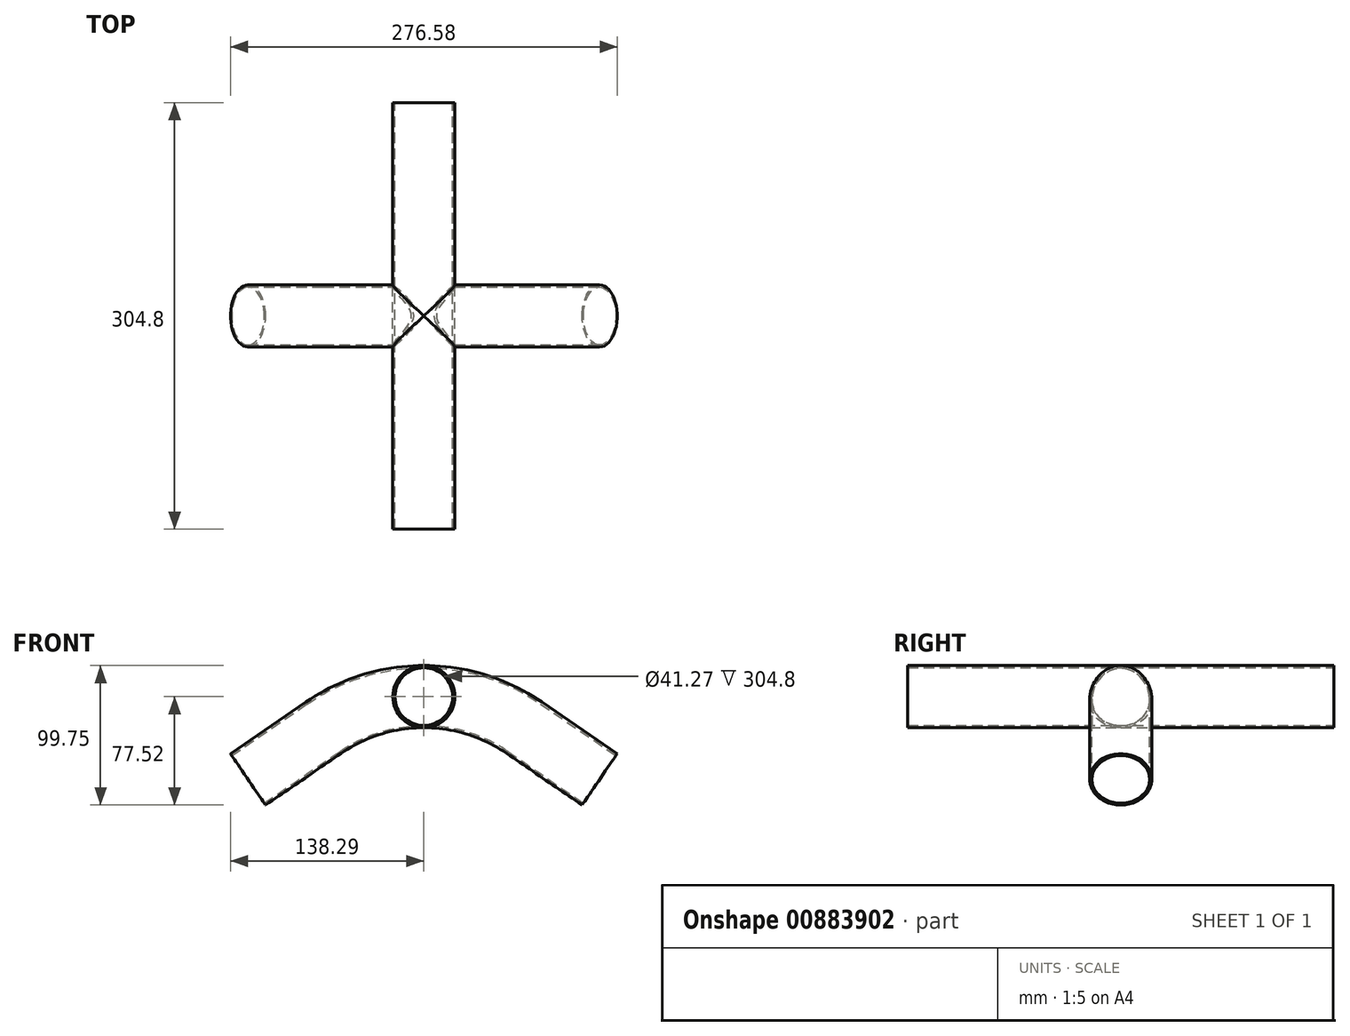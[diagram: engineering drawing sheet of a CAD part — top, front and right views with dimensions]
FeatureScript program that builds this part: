
annotation { "Feature Type Name" : "Feature", "Feature Type Description" : "" }
export const myFeature = defineFeature(function(context is Context, id is Id, definition is map)
    precondition{}
    {
        {
            var Q0;
            Q0=qCreatedBy(makeId("Front.planeOp"),FACE);
            var sketch = newSketch(context, id + "F0", { "sketchPlane" : qUnion([Q0])});
            skCircle(sketch, "E0", {"center": v(0, 0) * mm, "radius": 20.64 * mm});
            skCircle(sketch, "E1.0", {"center": v(0, 0) * mm, "radius": 22.23 * mm});
            skSolve(sketch);
        }
        {
            var Q0;
            Q0=makeQuery(id+"F0.imprint","IMPRINT",FACE,{"disambiguationData":[TD([[makeQuery(id+"F0.imprint","IMPRINT",EDGE,{"derivedFrom":sQuery(id+"F0.wireOp",EDGE,"E0")}),-1.0]])]});
            extrude(context, id + "F1", {"entities" : qUnion([Q0]), "endBound" : BoundingType.SYMMETRIC, "depth" : 304.8 * mm, "offsetDistance" : 25.4 * mm});
        }
        {
            var Q0;
            Q0=qCreatedBy(makeId("Front.planeOp"),FACE);
            var sketch = newSketch(context, id + "F2", { "sketchPlane" : qUnion([Q0])});
            skLineSegment(sketch, "E2", {"start": v(-125.73, -59.19) * mm, "end": v(-71.77, -22.23) * mm});
            skArc(sketch, "E3", {"start": v(-71.77, -22.23) * mm, "mid": v(0, 0) * mm, "end": v(71.77, -22.23) * mm});
            skLineSegment(sketch, "E4", {"start": v(71.77, -22.23) * mm, "end": v(125.73, -59.19) * mm});
            skLineSegment(sketch, "E5", {"start": v(-71.77, -22.23) * mm, "end": v(0, 26.94) * mm, "construction": true});
            skLineSegment(sketch, "E6", {"start": v(0, 26.94) * mm, "end": v(71.77, -22.23) * mm, "construction": true});
            skSolve(sketch);
        }
        {
            var Q0;
            Q0=sQuery(id+"F2.wireOp",VERTEX,"E2.start");
            var Q1;
            Q1=sQuery(id+"F2.wireOp",EDGE,"E2");
            cPlane(context, id + "F3", {"entities" : qUnion([Q0, Q1]), "cplaneType" : CPlaneType.LINE_POINT, "offset" : 25.4 * mm, "width" : 152.4 * mm, "height" : 152.4 * mm});
        }
        {
            var Q0;
            Q0=qCreatedBy(id+"F3.planeOp",FACE);
            var sketch = newSketch(context, id + "F4", { "sketchPlane" : qUnion([Q0])});
            skCircle(sketch, "E7", {"center": v(0, 22.23) * mm, "radius": 20.64 * mm});
            skCircle(sketch, "E8.0", {"center": v(0, 22.23) * mm, "radius": 22.23 * mm});
            skSolve(sketch);
        }
        {
            var Q0;
            Q0=makeQuery(id+"F4.imprint","IMPRINT",FACE,{"disambiguationData":[TD([[makeQuery(id+"F4.imprint","IMPRINT",EDGE,{"derivedFrom":sQuery(id+"F4.wireOp",EDGE,"E7")}),-1.0]])]});
            var Q1;
            Q1=sQuery(id+"F2.wireOp",EDGE,"E2");
            var Q2;
            Q2=sQuery(id+"F2.wireOp",EDGE,"E3");
            var Q3;
            Q3=sQuery(id+"F2.wireOp",EDGE,"E4");
            sweep(context, id + "F5", {"operationType" : NewBodyOperationType.ADD, "profiles" : qUnion([Q0]), "path" : qUnion([Q1, Q2, Q3])});
        }
        {
            var Q0;
            Q0=makeQuery(id+"F1.opExtrude","CAP_FACE",FACE,{"disambiguationData":[OSD([sQuery(id+"F0.wireOp",EDGE,"E0"),sQuery(id+"F0.wireOp",EDGE,"E1.0")])],"isStart":true});
            var sketch = newSketch(context, id + "F6", { "sketchPlane" : qUnion([Q0])});
            skCircle(sketch, "E9.0", {"center": v(0, 0) * mm, "radius": 20.64 * mm});
            skSolve(sketch);
        }
        {
            var Q0;
            Q0=makeQuery(id+"F6.imprint","IMPRINT",FACE,{"disambiguationData":[TD([[makeQuery(id+"F6.imprint","IMPRINT",EDGE,{"derivedFrom":sQuery(id+"F6.wireOp",EDGE,"E9.0")}),-1.0]])]});
            extrude(context, id + "F7", {"entities" : qUnion([Q0]), "operationType" : NewBodyOperationType.REMOVE, "endBound" : BoundingType.THROUGH_ALL, "oppositeDirection" : true, "depth" : 25.4 * mm, "offsetDistance" : 25.4 * mm});
        }
    });
